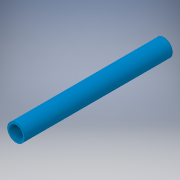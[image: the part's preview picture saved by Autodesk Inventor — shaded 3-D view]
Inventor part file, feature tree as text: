
AUTODESK INVENTOR PART (.ipt)
format: ipt  version: 2018 (Build 220112000, 112)  size: 105,984 bytes
history: native  units: in
note: dims shown in document units (in); Inventor stores cm internally (conversion verified against a paired STEP export)
features: extrude x1, sketch x1
ambient origin geometry x8: Origin, YZ Plane, XZ Plane, XY Plane, X Axis, Y Axis, Z Axis, Center Point
bodies: Solid1 (feature_tree)
feature tree (2):
  extrude  "Extrusion1"  Depth=11.25in
  sketch  "Sketch1"  dims[d0=1.315in d1=1.0in d2=11.25in d3=0.0in]
